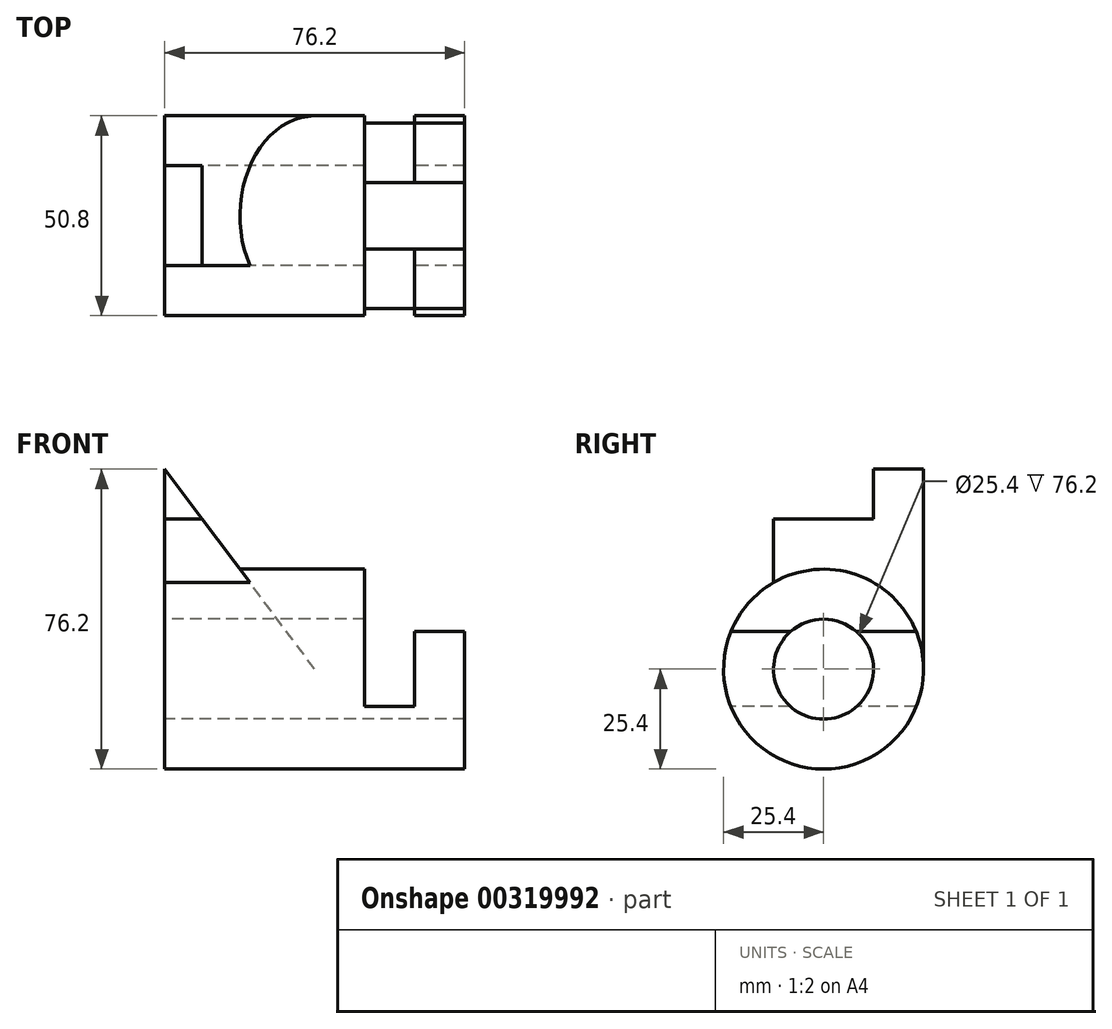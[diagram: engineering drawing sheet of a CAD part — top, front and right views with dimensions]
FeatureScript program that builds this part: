
annotation { "Feature Type Name" : "Feature", "Feature Type Description" : "" }
export const myFeature = defineFeature(function(context is Context, id is Id, definition is map)
    precondition{}
    {
        {
            var Q0;
            Q0=qCreatedBy(makeId("Right.planeOp"),FACE);
            var sketch = newSketch(context, id + "F0", { "sketchPlane" : qUnion([Q0])});
            skCircle(sketch, "E0", {"center": v(0, 0) * mm, "radius": 25.4 * mm});
            skCircle(sketch, "E1", {"center": v(0, 0) * mm, "radius": 12.7 * mm});
            skSolve(sketch);
        }
        {
            var Q0;
            Q0 = qSketchRegion(id + "F0", true);
            extrude(context, id + "F1", {"entities" : qUnion([Q0]), "depth" : 76.2 * mm});
        }
        {
            var Q0;
            Q0=qCreatedBy(makeId("Front.planeOp"),FACE);
            var sketch = newSketch(context, id + "F2", { "sketchPlane" : qUnion([Q0])});
            skLineSegment(sketch, "E2", {"start": v(-38.1, 25.4) * mm, "end": v(76.2, 25.4) * mm});
            skLineSegment(sketch, "E3", {"start": v(76.2, 25.4) * mm, "end": v(50.8, 25.4) * mm});
            skLineSegment(sketch, "E4", {"start": v(50.8, 25.4) * mm, "end": v(50.8, -9.52) * mm});
            skLineSegment(sketch, "E5", {"start": v(50.8, -9.52) * mm, "end": v(63.5, -9.52) * mm});
            skLineSegment(sketch, "E6", {"start": v(63.5, -9.52) * mm, "end": v(63.5, 9.53) * mm});
            skLineSegment(sketch, "E7", {"start": v(63.5, 9.53) * mm, "end": v(76.2, 9.53) * mm});
            skLineSegment(sketch, "E8", {"start": v(76.2, 9.53) * mm, "end": v(76.2, 25.4) * mm});
            skLineSegment(sketch, "E9.0", {"start": v(76.2, 25.4) * mm, "end": v(76.2, -25.4) * mm});
            skSolve(sketch);
        }
        {
            var Q0;
            Q0 = qSketchRegion(id + "F2", true);
            extrude(context, id + "F3", {"entities" : qUnion([Q0]), "operationType" : NewBodyOperationType.REMOVE, "endBound" : BoundingType.THROUGH_ALL, "oppositeDirection" : true, "depth" : 25.4 * mm, "hasSecondDirection" : true, "secondDirectionOppositeDirection" : false, "secondDirectionDepth" : 25.4 * mm});
        }
        {
            var Q0;
            Q0=qCreatedBy(makeId("Front.planeOp"),FACE);
            var sketch = newSketch(context, id + "F4", { "sketchPlane" : qUnion([Q0])});
            skLineSegment(sketch, "E10", {"start": v(0, 0) * mm, "end": v(38.1, 0) * mm});
            skLineSegment(sketch, "E11", {"start": v(38.1, 0) * mm, "end": v(0, 50.8) * mm});
            skLineSegment(sketch, "E12", {"start": v(0, 50.8) * mm, "end": v(0, 0) * mm});
            skSolve(sketch);
        }
        {
            var Q0;
            Q0 = qSketchRegion(id + "F4", true);
            extrude(context, id + "F5", {"entities" : qUnion([Q0]), "operationType" : NewBodyOperationType.ADD, "oppositeDirection" : true, "depth" : 25.4 * mm, "hasSecondDirection" : true, "secondDirectionOppositeDirection" : false, "secondDirectionDepth" : 12.7 * mm});
        }
        {
            var Q0;
            Q0=qCreatedBy(makeId("Front.planeOp"),FACE);
            var sketch = newSketch(context, id + "F6", { "sketchPlane" : qUnion([Q0])});
            skLineSegment(sketch, "E13", {"start": v(0, 38.1) * mm, "end": v(9.52, 38.1) * mm});
            skLineSegment(sketch, "E14", {"start": v(9.52, 38.1) * mm, "end": v(0, 50.8) * mm});
            skLineSegment(sketch, "E15", {"start": v(0, 50.8) * mm, "end": v(0, 38.1) * mm});
            skPoint(sketch, "E16.0", {"position": v(0, 50.8) * mm});
            skLineSegment(sketch, "E17.0", {"start": v(21.6, 22) * mm, "end": v(0, 50.8) * mm});
            skSolve(sketch);
        }
        {
            var Q0;
            Q0 = qSketchRegion(id + "F6", true);
            extrude(context, id + "F7", {"entities" : qUnion([Q0]), "operationType" : NewBodyOperationType.REMOVE, "depth" : 25.4 * mm, "hasSecondDirection" : true, "secondDirectionOppositeDirection" : true, "secondDirectionDepth" : 12.7 * mm});
        }
        {
            var Q0;
            Q0=qCreatedBy(makeId("Right.planeOp"),FACE);
            var sketch = newSketch(context, id + "F8", { "sketchPlane" : qUnion([Q0])});
            skCircle(sketch, "E18", {"center": v(0, 0) * mm, "radius": 12.7 * mm});
            skSolve(sketch);
        }
        {
            var Q0;
            Q0 = qSketchRegion(id + "F8", true);
            extrude(context, id + "F9", {"entities" : qUnion([Q0]), "operationType" : NewBodyOperationType.REMOVE, "endBound" : BoundingType.THROUGH_ALL, "depth" : 25.4 * mm});
        }
    });
